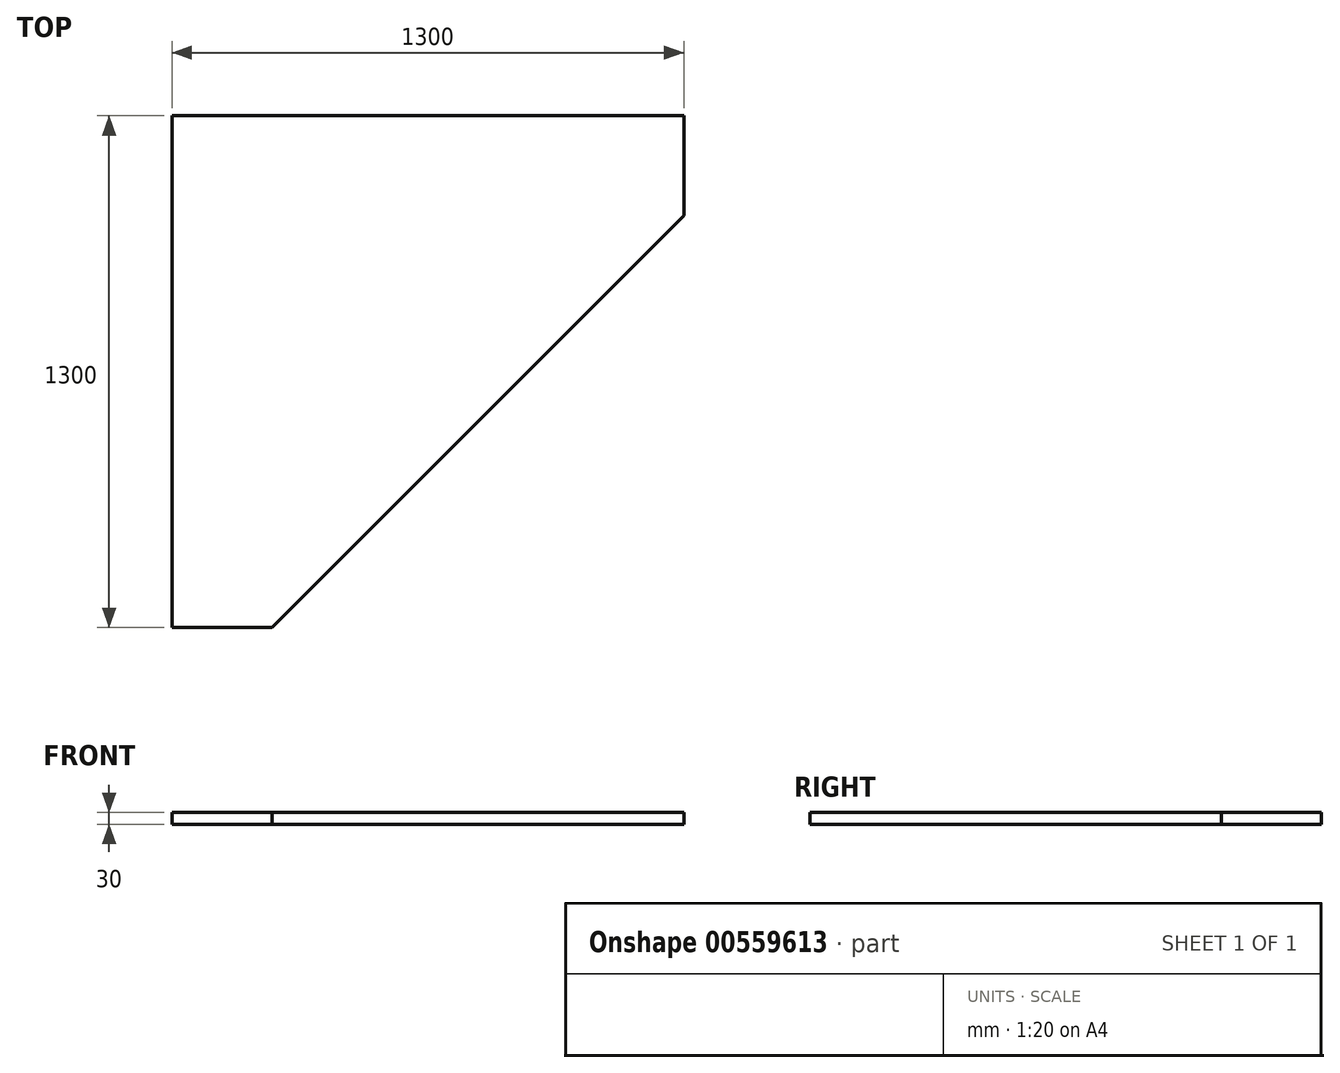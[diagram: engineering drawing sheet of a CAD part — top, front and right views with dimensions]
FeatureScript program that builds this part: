
annotation { "Feature Type Name" : "Feature", "Feature Type Description" : "" }
export const myFeature = defineFeature(function(context is Context, id is Id, definition is map)
    precondition{}
    {
        {
            var Q0;
            Q0=qCreatedBy(makeId("Top.planeOp"),FACE);
            var sketch = newSketch(context, id + "F0", { "sketchPlane" : qUnion([Q0])});
            skLineSegment(sketch, "E0.bottom", {"start": v(635, 635) * mm, "end": v(-635, 635) * mm});
            skLineSegment(sketch, "E0.top", {"start": v(635, -635) * mm, "end": v(-635, -635) * mm, "construction": true});
            skLineSegment(sketch, "E0.left", {"start": v(635, 635) * mm, "end": v(635, -635) * mm, "construction": true});
            skLineSegment(sketch, "E0.right", {"start": v(-635, 635) * mm, "end": v(-635, -635) * mm});
            skPoint(sketch, "E0.middle", {"position": v(0, 0) * mm});
            skLineSegment(sketch, "E1", {"start": v(-635, -635) * mm, "end": v(-351, -635) * mm, "construction": true});
            skLineSegment(sketch, "E2", {"start": v(-351, -635) * mm, "end": v(635, 351) * mm});
            skLineSegment(sketch, "E3", {"start": v(635, 351) * mm, "end": v(635, 635) * mm, "construction": true});
            skLineSegment(sketch, "E4", {"start": v(635, 351) * mm, "end": v(919, 635) * mm, "construction": true});
            skLineSegment(sketch, "E5", {"start": v(919, 635) * mm, "end": v(635, 635) * mm, "construction": true});
            skLineSegment(sketch, "E6", {"start": v(-635, -635) * mm, "end": v(-635, -665) * mm});
            skLineSegment(sketch, "E7", {"start": v(-635, -665) * mm, "end": v(-381, -665) * mm});
            skLineSegment(sketch, "E8", {"start": v(-381, -665) * mm, "end": v(-351, -635) * mm});
            skLineSegment(sketch, "E9", {"start": v(635, 635) * mm, "end": v(665, 635) * mm});
            skLineSegment(sketch, "E10", {"start": v(665, 635) * mm, "end": v(665, 381) * mm});
            skLineSegment(sketch, "E11", {"start": v(665, 381) * mm, "end": v(635, 351) * mm});
            skSolve(sketch);
        }
        {
            var Q0;
            Q0 = qSketchRegion(id + "F0", true);
            extrude(context, id + "F1", {"entities" : qUnion([Q0]), "depth" : 30 * mm, "offsetDistance" : 25.4 * mm});
        }
    });
